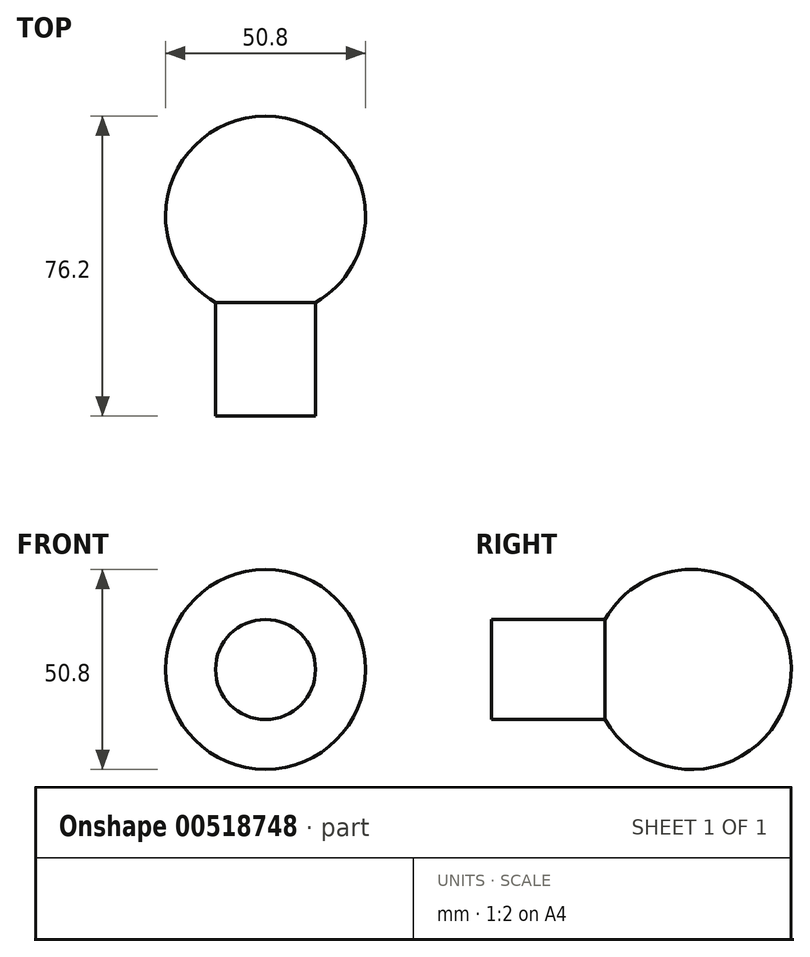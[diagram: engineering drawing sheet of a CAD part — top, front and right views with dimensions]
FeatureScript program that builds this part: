
annotation { "Feature Type Name" : "Feature", "Feature Type Description" : "" }
export const myFeature = defineFeature(function(context is Context, id is Id, definition is map)
    precondition{}
    {
        {
            var Q0;
            Q0=qCreatedBy(makeId("Front.planeOp"),FACE);
            var sketch = newSketch(context, id + "F0", { "sketchPlane" : qUnion([Q0])});
            skLineSegment(sketch, "E0", {"start": v(25.4, 0) * mm, "end": v(-25.4, 0) * mm});
            skArc(sketch, "E1", {"start": v(25.4, 0) * mm, "mid": v(0, 25.4) * mm, "end": v(-25.4, 0) * mm});
            skSolve(sketch);
        }
        {
            var Q0;
            Q0=makeQuery(id+"F0.imprint","IMPRINT",FACE,{"disambiguationData":[TD([[makeQuery(id+"F0.imprint","IMPRINT",EDGE,{"derivedFrom":sQuery(id+"F0.wireOp",EDGE,"E0")}),-1.0]])]});
            var Q1;
            Q1=sQuery(id+"F0.wireOp",EDGE,"E0");
            revolve(context, id + "F1", {"entities" : qUnion([Q0]), "axis" : qUnion([Q1]), "revolveType" : RevolveType.FULL});
        }
        {
            var Q0;
            Q0=qCreatedBy(makeId("Front.planeOp"),FACE);
            var sketch = newSketch(context, id + "F2", { "sketchPlane" : qUnion([Q0])});
            skCircle(sketch, "E2", {"center": v(0, 0) * mm, "radius": 12.7 * mm});
            skSolve(sketch);
        }
        {
            var Q0;
            Q0 = qSketchRegion(id + "F2", true);
            extrude(context, id + "F3", {"entities" : qUnion([Q0]), "operationType" : NewBodyOperationType.ADD, "depth" : 50.8 * mm, "offsetDistance" : 25.4 * mm});
        }
    });
